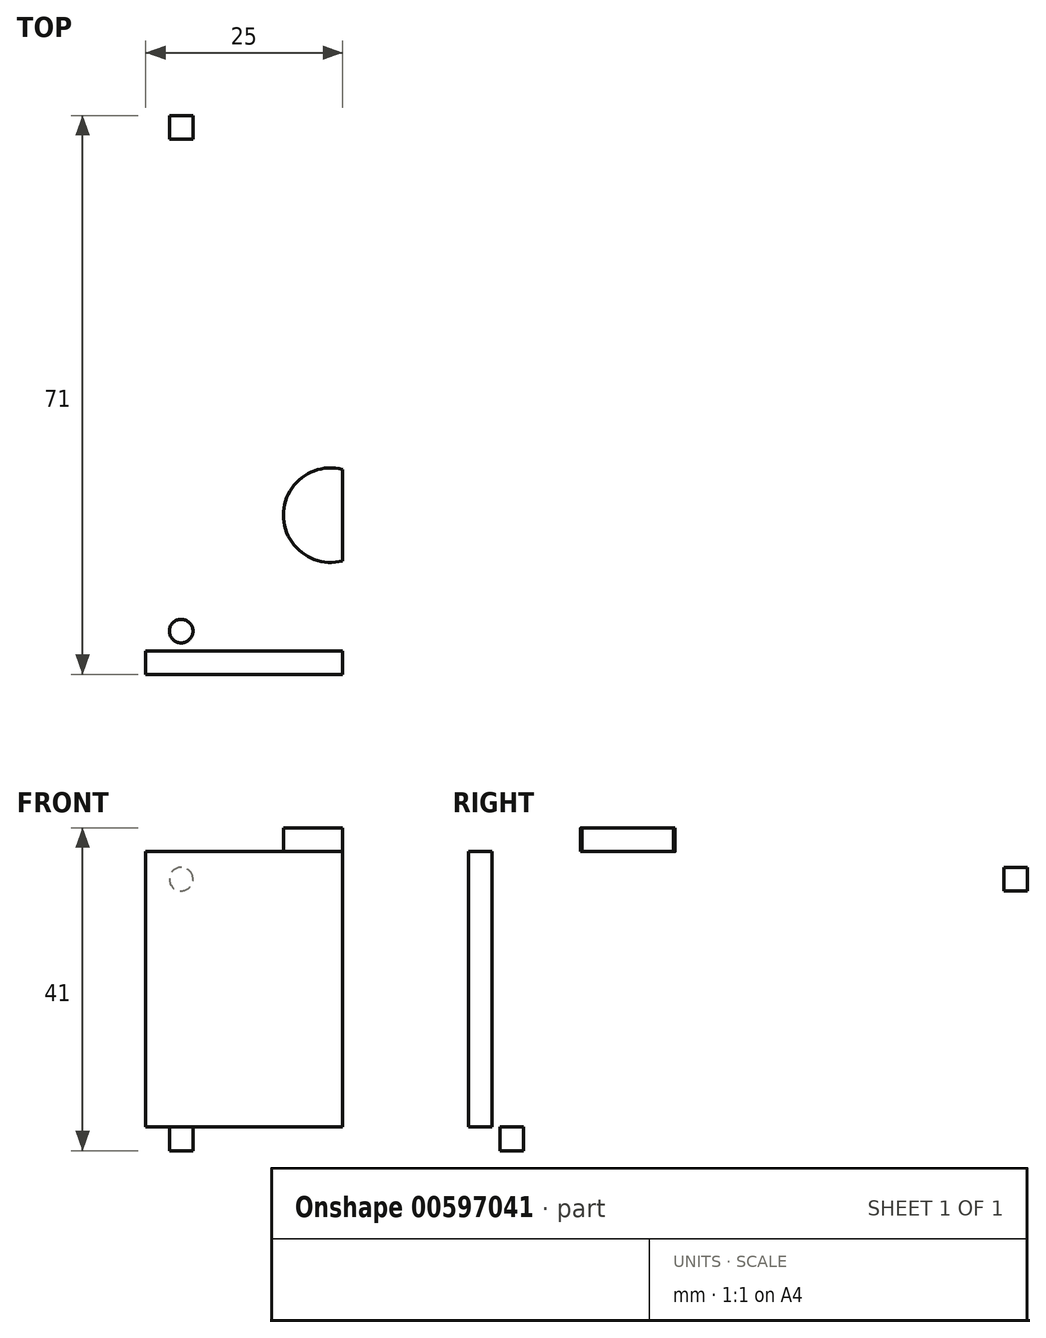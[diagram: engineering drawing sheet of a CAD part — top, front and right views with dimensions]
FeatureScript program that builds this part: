
annotation { "Feature Type Name" : "Feature", "Feature Type Description" : "" }
export const myFeature = defineFeature(function(context is Context, id is Id, definition is map)
    precondition{}
    {
        {
            var Q0;
            Q0=qCreatedBy(makeId("Right.planeOp"),FACE);
            var sketch = newSketch(context, id + "F0", { "sketchPlane" : qUnion([Q0])});
            skLineSegment(sketch, "E0", {"start": v(0, 0) * mm, "end": v(-7, 0) * mm});
            skLineSegment(sketch, "E1", {"start": v(-7, 0) * mm, "end": v(-7, 35) * mm});
            skLineSegment(sketch, "E2", {"start": v(-7, 35) * mm, "end": v(58, 35) * mm});
            skLineSegment(sketch, "E3", {"start": v(58, 35) * mm, "end": v(58, 27) * mm});
            skLineSegment(sketch, "E4", {"start": v(0, 0) * mm, "end": v(0, -3) * mm});
            skLineSegment(sketch, "E5", {"start": v(0, -3) * mm, "end": v(-10, -3) * mm});
            skLineSegment(sketch, "E6", {"start": v(-10, -3) * mm, "end": v(-10, 38) * mm});
            skLineSegment(sketch, "E7", {"start": v(-10, 38) * mm, "end": v(61, 38) * mm});
            skLineSegment(sketch, "E8", {"start": v(58, 27) * mm, "end": v(61, 27) * mm});
            skLineSegment(sketch, "E9", {"start": v(61, 38) * mm, "end": v(61, 27) * mm});
            skSolve(sketch);
        }
        {
            var Q0;
            Q0=makeQuery(id+"F0.imprint","IMPRINT",FACE,{"disambiguationData":[TD([[makeQuery(id+"F0.imprint","IMPRINT",EDGE,{"derivedFrom":sQuery(id+"F0.wireOp",EDGE,"E0")}),1.0]])]});
            extrude(context, id + "F1", {"entities" : qUnion([Q0]), "depth" : 25 * mm, "offsetDistance" : 25.4 * mm});
        }
        {
            var Q0;
            Q0=makeQuery(id+"F1.opExtrude","SWEPT_FACE",FACE,{"disambiguationData":[OSD([sQuery(id+"F0.wireOp",EDGE,"E5")])]});
            var sketch = newSketch(context, id + "F2", { "sketchPlane" : qUnion([Q0])});
            skLineSegment(sketch, "E10", {"start": v(12.5, 10) * mm, "end": v(12.5, 0) * mm, "construction": true});
            skCircle(sketch, "E11", {"center": v(20.5, 4.5) * mm, "radius": 1.5 * mm});
            skCircle(sketch, "E12.MirrorC", {"center": v(4.5, 4.5) * mm, "radius": 1.5 * mm});
            skSolve(sketch);
        }
        {
            var Q0;
            Q0=makeQuery(id+"F2.imprint","IMPRINT",FACE,{"disambiguationData":[TD([[makeQuery(id+"F2.imprint","IMPRINT",EDGE,{"derivedFrom":sQuery(id+"F2.wireOp",EDGE,"E11")}),1.0]])]});
            var Q1;
            Q1=makeQuery(id+"F2.imprint","IMPRINT",FACE,{"disambiguationData":[TD([[makeQuery(id+"F2.imprint","IMPRINT",EDGE,{"derivedFrom":sQuery(id+"F2.wireOp",EDGE,"E12.MirrorC")}),-1.0]])]});
            extrude(context, id + "F3", {"entities" : qUnion([Q0, Q1]), "operationType" : NewBodyOperationType.REMOVE, "oppositeDirection" : true, "depth" : 3 * mm, "offsetDistance" : 25.4 * mm});
        }
        {
            var Q0;
            Q0=makeQuery(id+"F1.opExtrude","SWEPT_FACE",FACE,{"disambiguationData":[OSD([sQuery(id+"F0.wireOp",EDGE,"E9")])]});
            var sketch = newSketch(context, id + "F4", { "sketchPlane" : qUnion([Q0])});
            skLineSegment(sketch, "E13", {"start": v(-12.5, 38) * mm, "end": v(-12.5, 27) * mm, "construction": true});
            skCircle(sketch, "E14", {"center": v(-20.5, 31.5) * mm, "radius": 1.5 * mm});
            skCircle(sketch, "E15.MirrorC", {"center": v(-4.5, 31.5) * mm, "radius": 1.5 * mm});
            skSolve(sketch);
        }
        {
            var Q0;
            Q0=makeQuery(id+"F4.imprint","IMPRINT",FACE,{"disambiguationData":[TD([[makeQuery(id+"F4.imprint","IMPRINT",EDGE,{"derivedFrom":sQuery(id+"F4.wireOp",EDGE,"E14")}),1.0]])]});
            var Q1;
            Q1=makeQuery(id+"F4.imprint","IMPRINT",FACE,{"disambiguationData":[TD([[makeQuery(id+"F4.imprint","IMPRINT",EDGE,{"derivedFrom":sQuery(id+"F4.wireOp",EDGE,"E15.MirrorC")}),-1.0]])]});
            extrude(context, id + "F5", {"entities" : qUnion([Q0, Q1]), "operationType" : NewBodyOperationType.REMOVE, "oppositeDirection" : true, "depth" : 3 * mm, "offsetDistance" : 25.4 * mm});
        }
        {
            var Q0;
            Q0=makeQuery(id+"F1.opExtrude","SWEPT_FACE",FACE,{"disambiguationData":[OSD([sQuery(id+"F0.wireOp",EDGE,"E7")])]});
            var sketch = newSketch(context, id + "F6", { "sketchPlane" : qUnion([Q0])});
            skLineSegment(sketch, "E16.bottom", {"start": v(12.5, 61) * mm, "end": v(-15, 61) * mm});
            skLineSegment(sketch, "E16.top", {"start": v(12.5, -10) * mm, "end": v(-15, -10) * mm});
            skLineSegment(sketch, "E16.left", {"start": v(12.5, 61) * mm, "end": v(12.5, -10) * mm});
            skLineSegment(sketch, "E16.right", {"start": v(-15, 61) * mm, "end": v(-15, -10) * mm});
            skLineSegment(sketch, "E17", {"start": v(12.5, 10.24) * mm, "end": v(-15, 10.24) * mm, "construction": true});
            skLineSegment(sketch, "E18", {"start": v(1.5, 61) * mm, "end": v(1.5, -10) * mm});
            skLineSegment(sketch, "E19", {"start": v(0, 61) * mm, "end": v(0, -10) * mm});
            skCircle(sketch, "E20", {"center": v(1.5, 10.24) * mm, "radius": 6 * mm});
            skCircle(sketch, "E21", {"center": v(1.5, 10.24) * mm, "radius": 4 * mm});
            skLineSegment(sketch, "E22.bottom", {"start": v(12.5, 20.24) * mm, "end": v(-15, 20.24) * mm});
            skLineSegment(sketch, "E22.top", {"start": v(12.5, 0.24) * mm, "end": v(-15, 0.24) * mm});
            skLineSegment(sketch, "E22.left", {"start": v(12.5, 20.24) * mm, "end": v(12.5, 0.24) * mm});
            skLineSegment(sketch, "E22.right", {"start": v(-15, 20.24) * mm, "end": v(-15, 0.24) * mm});
            skLineSegment(sketch, "E23.MirrorCS", {"start": v(12.5, 20.24) * mm, "end": v(40, 20.24) * mm});
            skLineSegment(sketch, "E24.MirrorCS", {"start": v(12.5, 0.24) * mm, "end": v(40, 0.24) * mm});
            skLineSegment(sketch, "E25.MirrorCS", {"start": v(40, 61) * mm, "end": v(40, -10) * mm});
            skCircle(sketch, "E26.MirrorC", {"center": v(23.5, 10.24) * mm, "radius": 6 * mm});
            skCircle(sketch, "E27.MirrorC", {"center": v(23.5, 10.24) * mm, "radius": 4 * mm});
            skLineSegment(sketch, "E28.MirrorCS", {"start": v(12.5, -10) * mm, "end": v(40, -10) * mm});
            skSolve(sketch);
        }
        {
            var Q0;
            {var subQ0=sQuery(id+"F6.wireOp",EDGE,"E22.right");Q0=makeQuery(id+"F6.imprint","IMPRINT",FACE,{"disambiguationData":[TD([[makeQuery(id+"F6.imprint","IMPRINT",EDGE,{"derivedFrom":subQ0}),1.0]])]});}
            var Q1;
            {var subQ0=sQuery(id+"F6.wireOp",EDGE,"E21");var subQ1=sQuery(id+"F6.wireOp",EDGE,"E19");var subQ2=makeQuery(id+"F6.imprint","INTERSECT",VERTEX,{"disambiguationData":[OD(0.0)],"derivedFrom":[subQ1,subQ0]});Q1=makeQuery(id+"F6.imprint","IMPRINT",FACE,{"disambiguationData":[TD([[makeQuery(id+"F6.imprint","IMPRINT",EDGE,{"disambiguationData":[TD([[subQ2,-1.0]])],"derivedFrom":subQ1}),1.0]])]});}
            var Q2;
            {var subQ0=sQuery(id+"F6.wireOp",EDGE,"E20");var subQ1=sQuery(id+"F6.wireOp",EDGE,"E19");var subQ2=makeQuery(id+"F6.imprint","INTERSECT",VERTEX,{"disambiguationData":[OD(0.0)],"derivedFrom":[subQ1,subQ0]});Q2=makeQuery(id+"F6.imprint","IMPRINT",FACE,{"disambiguationData":[TD([[makeQuery(id+"F6.imprint","IMPRINT",EDGE,{"disambiguationData":[TD([[subQ2,-1.0]])],"derivedFrom":subQ1}),1.0]])]});}
            var Q3;
            {var subQ0=sQuery(id+"F6.wireOp",EDGE,"E25.MirrorCS");var subQ1=sQuery(id+"F6.wireOp",EDGE,"E23.MirrorCS");var subQ2=makeQuery(id+"F6.imprint","INTERSECT",VERTEX,{"derivedFrom":[subQ1,subQ0]});Q3=makeQuery(id+"F6.imprint","IMPRINT",FACE,{"disambiguationData":[TD([[makeQuery(id+"F6.imprint","IMPRINT",EDGE,{"disambiguationData":[TD([[subQ2,1.0]])],"derivedFrom":subQ1}),-1.0]])]});}
            var Q4;
            {var subQ0=sQuery(id+"F6.wireOp",EDGE,"E26.MirrorC");var subQ1=makeQuery(id+"F1.opExtrude","CAP_EDGE",EDGE,{"disambiguationData":[OSD([sQuery(id+"F0.wireOp",EDGE,"E7")])],"isStart":false});var subQ2=makeQuery(id+"F6.imprint","INTERSECT",VERTEX,{"disambiguationData":[OD(0.0)],"derivedFrom":[subQ1,subQ0]});Q4=makeQuery(id+"F6.imprint","IMPRINT",FACE,{"disambiguationData":[TD([[makeQuery(id+"F6.imprint","IMPRINT",EDGE,{"disambiguationData":[TD([[subQ2,-1.0]])],"derivedFrom":subQ0}),-1.0]])]});}
            var Q5;
            {var subQ0=sQuery(id+"F6.wireOp",EDGE,"E27.MirrorC");var subQ1=makeQuery(id+"F1.opExtrude","CAP_EDGE",EDGE,{"disambiguationData":[OSD([sQuery(id+"F0.wireOp",EDGE,"E7")])],"isStart":false});var subQ2=makeQuery(id+"F6.imprint","INTERSECT",VERTEX,{"disambiguationData":[OD(0.0)],"derivedFrom":[subQ1,subQ0]});Q5=makeQuery(id+"F6.imprint","IMPRINT",FACE,{"disambiguationData":[TD([[makeQuery(id+"F6.imprint","IMPRINT",EDGE,{"disambiguationData":[TD([[subQ2,-1.0]])],"derivedFrom":subQ0}),-1.0]])]});}
            extrude(context, id + "F7", {"entities" : qUnion([Q0, Q1, Q2, Q3, Q4, Q5]), "operationType" : NewBodyOperationType.ADD, "oppositeDirection" : true, "depth" : 3 * mm, "offsetDistance" : 25.4 * mm});
        }
        {
            var Q0;
            Q0=makeQuery(id+"F7.boolean.opBoolean","MERGE",FACE,{"derivedFrom":[makeQuery(id+"F1.opExtrude","SWEPT_FACE",FACE,{"disambiguationData":[OSD([sQuery(id+"F0.wireOp",EDGE,"E7")])]}),makeQuery(id+"F7.opExtrude","CAP_FACE",FACE,{"disambiguationData":[OSD([sQuery(id+"F6.wireOp",EDGE,"E19"),sQuery(id+"F6.wireOp",EDGE,"E22.bottom"),sQuery(id+"F6.wireOp",EDGE,"E22.top"),sQuery(id+"F6.wireOp",EDGE,"E22.right")])],"isStart":true})]});
            var sketch = newSketch(context, id + "F8", { "sketchPlane" : qUnion([Q0])});
            skCircle(sketch, "E29", {"center": v(1.5, 10.24) * mm, "radius": 6 * mm});
            skPoint(sketch, "E29.centerSnap0", {"position": v(-15, 10.24) * mm});
            skLineSegment(sketch, "E30", {"start": v(12.5, 61) * mm, "end": v(12.5, -10) * mm, "construction": true});
            skCircle(sketch, "E31.MirrorC", {"center": v(23.5, 10.24) * mm, "radius": 6 * mm});
            skSolve(sketch);
        }
        {
            var Q0;
            Q0=makeQuery(id+"F8.imprint","IMPRINT",FACE,{"disambiguationData":[TD([[makeQuery(id+"F8.imprint","IMPRINT",EDGE,{"derivedFrom":sQuery(id+"F8.wireOp",EDGE,"E29")}),1.0]])]});
            var Q1;
            Q1=makeQuery(id+"F8.imprint","IMPRINT",FACE,{"disambiguationData":[TD([[makeQuery(id+"F8.imprint","IMPRINT",EDGE,{"derivedFrom":sQuery(id+"F8.wireOp",EDGE,"E31.MirrorC")}),-1.0]])]});
            extrude(context, id + "F9", {"entities" : qUnion([Q0, Q1]), "operationType" : NewBodyOperationType.REMOVE, "oppositeDirection" : true, "depth" : 3 * mm, "offsetDistance" : 25.4 * mm});
        }
    });
